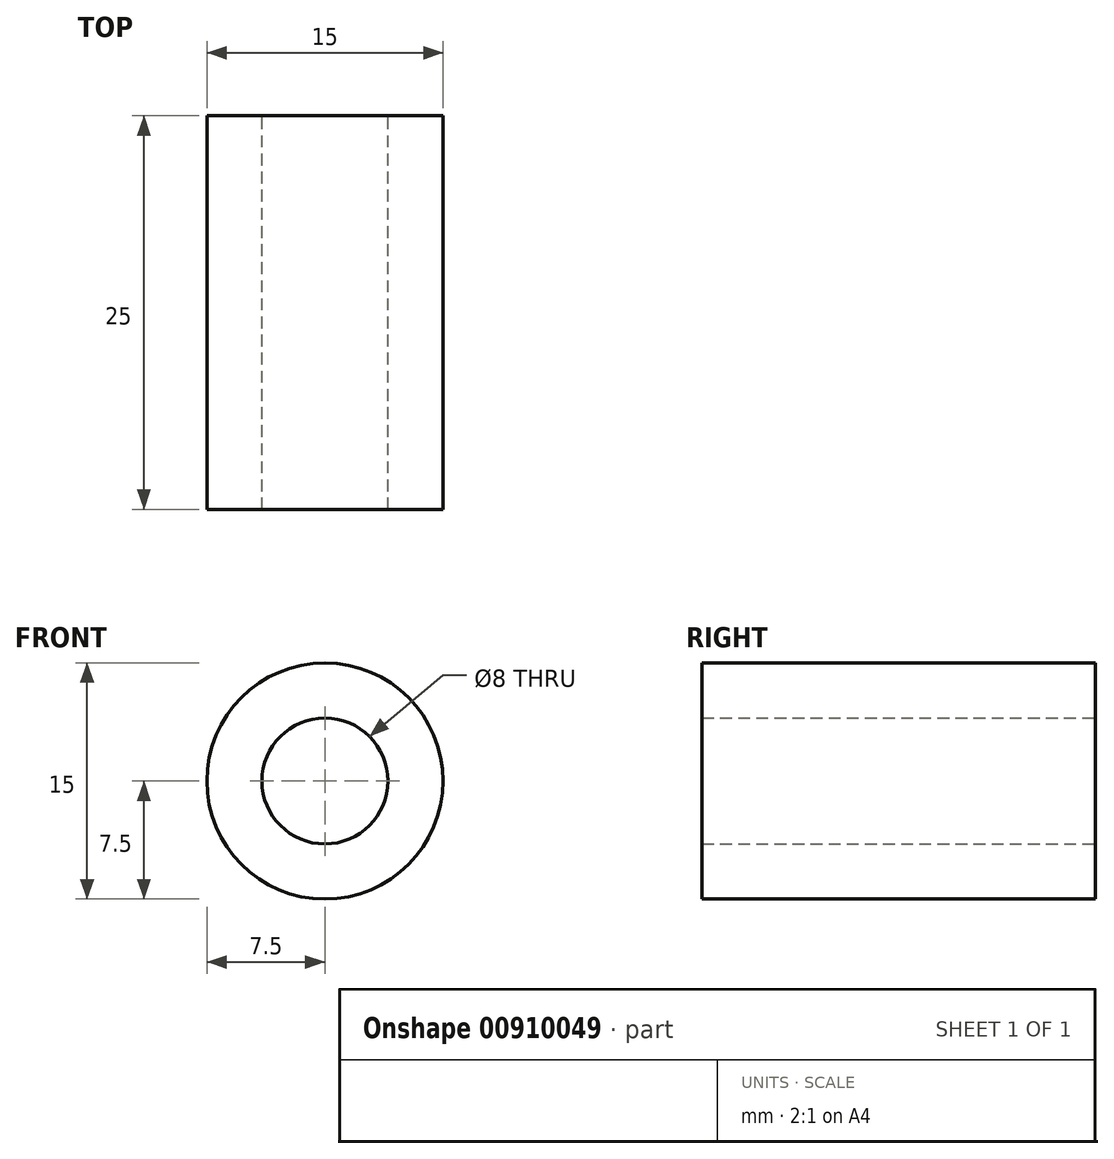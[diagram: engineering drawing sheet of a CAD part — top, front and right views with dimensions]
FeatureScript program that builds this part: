
annotation { "Feature Type Name" : "Feature", "Feature Type Description" : "" }
export const myFeature = defineFeature(function(context is Context, id is Id, definition is map)
    precondition{}
    {
        {
            var Q0;
            Q0=qCreatedBy(makeId("Front.planeOp"),FACE);
            var sketch = newSketch(context, id + "F0", { "sketchPlane" : qUnion([Q0])});
            skCircle(sketch, "E0", {"center": v(0, 0) * mm, "radius": 7.5 * mm});
            skCircle(sketch, "E1", {"center": v(0, 0) * mm, "radius": 4 * mm});
            skSolve(sketch);
        }
        {
            var Q0;
            Q0=makeQuery(id+"F0.imprint","IMPRINT",FACE,{"disambiguationData":[TD([[makeQuery(id+"F0.imprint","IMPRINT",EDGE,{"derivedFrom":sQuery(id+"F0.wireOp",EDGE,"E0")}),1.0]])]});
            extrude(context, id + "F1", {"entities" : qUnion([Q0]), "depth" : 25 * mm, "offsetDistance" : 25 * mm});
        }
    });
